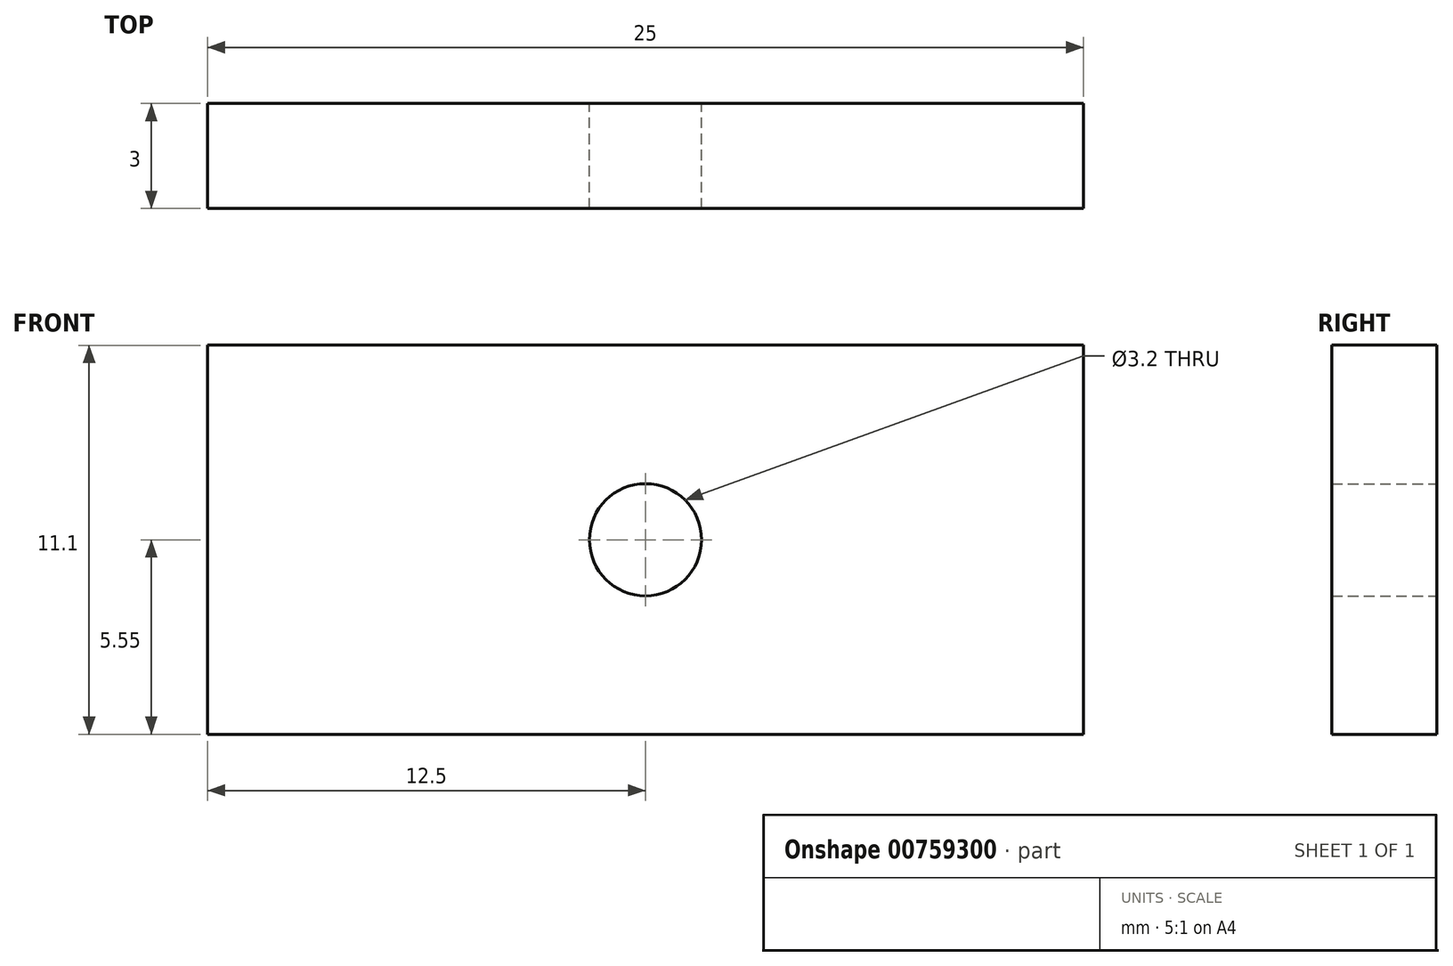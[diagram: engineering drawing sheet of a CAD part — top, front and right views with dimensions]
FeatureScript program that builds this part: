
annotation { "Feature Type Name" : "Feature", "Feature Type Description" : "" }
export const myFeature = defineFeature(function(context is Context, id is Id, definition is map)
    precondition{}
    {
        {
            var Q0;
            Q0=qCreatedBy(makeId("Front.planeOp"),FACE);
            var sketch = newSketch(context, id + "F0", { "sketchPlane" : qUnion([Q0])});
            skLineSegment(sketch, "E0.bottom", {"start": v(-12.5, 5.55) * mm, "end": v(12.5, 5.55) * mm});
            skLineSegment(sketch, "E0.top", {"start": v(-12.5, -5.55) * mm, "end": v(12.5, -5.55) * mm});
            skLineSegment(sketch, "E0.left", {"start": v(-12.5, 5.55) * mm, "end": v(-12.5, -5.55) * mm});
            skLineSegment(sketch, "E0.right", {"start": v(12.5, 5.55) * mm, "end": v(12.5, -5.55) * mm});
            skPoint(sketch, "E0.middle", {"position": v(0, 0) * mm});
            skCircle(sketch, "E1", {"center": v(0, 0) * mm, "radius": 1.6 * mm});
            skSolve(sketch);
        }
        {
            var Q0;
            Q0 = qSketchRegion(id + "F0", true);
            extrude(context, id + "F1", {"entities" : qUnion([Q0]), "depth" : 3 * mm, "offsetDistance" : 25 * mm});
        }
    });
